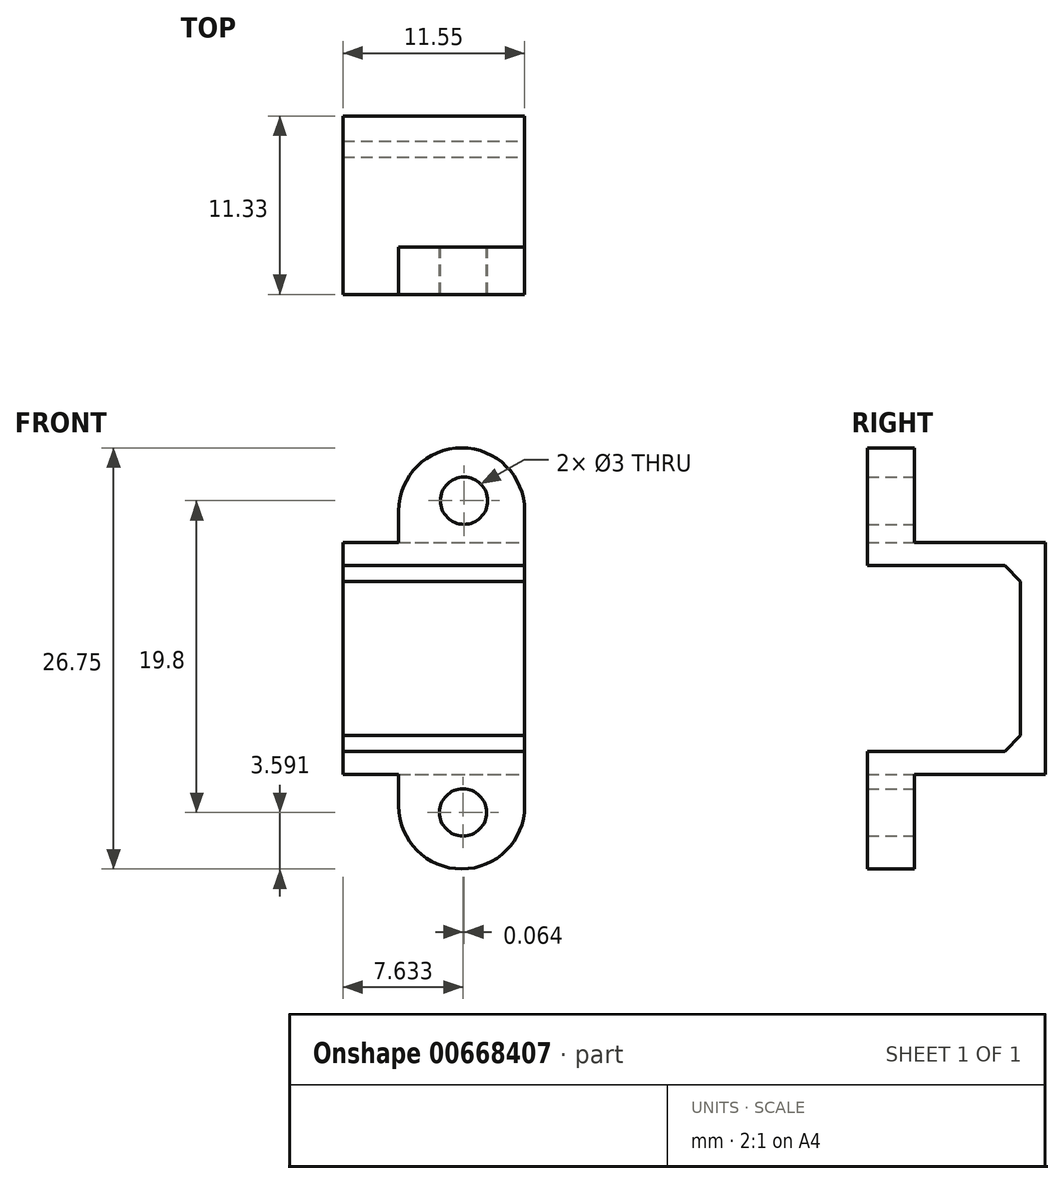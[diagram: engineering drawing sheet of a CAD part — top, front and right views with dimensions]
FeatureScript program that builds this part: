
annotation { "Feature Type Name" : "Feature", "Feature Type Description" : "" }
export const myFeature = defineFeature(function(context is Context, id is Id, definition is map)
    precondition{}
    {
        {
            var Q0;
            Q0=qCreatedBy(makeId("Front.planeOp"),FACE);
            var sketch = newSketch(context, id + "F0", { "sketchPlane" : qUnion([Q0])});
            skLineSegment(sketch, "E0.bottom", {"start": v(0, 0) * mm, "end": v(11.55, 0) * mm});
            skLineSegment(sketch, "E0.top", {"start": v(0, 14.75) * mm, "end": v(11.55, 14.75) * mm});
            skLineSegment(sketch, "E0.left", {"start": v(0, 0) * mm, "end": v(0, 14.75) * mm});
            skLineSegment(sketch, "E0.right", {"start": v(11.55, 0) * mm, "end": v(11.55, 14.75) * mm});
            skLineSegment(sketch, "E1", {"start": v(0, 14.75) * mm, "end": v(0, 13.27) * mm});
            skLineSegment(sketch, "E2", {"start": v(0, 13.27) * mm, "end": v(11.55, 13.27) * mm});
            skLineSegment(sketch, "E3", {"start": v(0, 0) * mm, "end": v(0, 1.48) * mm});
            skLineSegment(sketch, "E4", {"start": v(0, 1.48) * mm, "end": v(11.55, 1.48) * mm});
            skLineSegment(sketch, "E5", {"start": v(11.55, 1.48) * mm, "end": v(11.55, 0) * mm});
            skSolve(sketch);
        }
        {
            var Q0;
            Q0=makeQuery(id+"F0.imprint","IMPRINT",FACE,{"disambiguationData":[TD([[makeQuery(id+"F0.imprint","IMPRINT",EDGE,{"derivedFrom":sQuery(id+"F0.wireOp",EDGE,"E0.bottom")}),1.0]])]});
            var Q1;
            {var subQ0=sQuery(id+"F0.wireOp",EDGE,"E0.top");Q1=makeQuery(id+"F0.imprint","IMPRINT",FACE,{"disambiguationData":[TD([[makeQuery(id+"F0.imprint","IMPRINT",EDGE,{"derivedFrom":subQ0}),-1.0]])]});}
            var Q2;
            Q2=makeQuery(id+"F0.imprint","IMPRINT",FACE,{"disambiguationData":[TD([[makeQuery(id+"F0.imprint","IMPRINT",EDGE,{"derivedFrom":sQuery(id+"F0.wireOp",EDGE,"E0.left")}),-1.0]])]});
            extrude(context, id + "F1", {"entities" : qUnion([Q0, Q1, Q2]), "depth" : 11.33 * mm, "offsetDistance" : 25 * mm});
        }
        {
            var Q0;
            Q0=makeQuery(id+"F1.opExtrude","CAP_FACE",FACE,{"disambiguationData":[OSD([sQuery(id+"F0.wireOp",EDGE,"E0.bottom"),sQuery(id+"F0.wireOp",EDGE,"E0.top"),sQuery(id+"F0.wireOp",EDGE,"E0.left"),sQuery(id+"F0.wireOp",EDGE,"E0.right"),sQuery(id+"F0.wireOp",EDGE,"E1"),sQuery(id+"F0.wireOp",EDGE,"E3"),sQuery(id+"F0.wireOp",EDGE,"E5")])],"isStart":false});
            var sketch = newSketch(context, id + "F2", { "sketchPlane" : qUnion([Q0])});
            skLineSegment(sketch, "E6", {"start": v(0, 14.75) * mm, "end": v(0, 13.27) * mm});
            skLineSegment(sketch, "E7", {"start": v(0, 13.27) * mm, "end": v(11.55, 13.27) * mm});
            skLineSegment(sketch, "E8", {"start": v(0, 0) * mm, "end": v(0, 1.48) * mm});
            skLineSegment(sketch, "E9", {"start": v(0, 1.48) * mm, "end": v(11.55, 1.48) * mm});
            skLineSegment(sketch, "E10", {"start": v(0, 13.27) * mm, "end": v(0, 1.48) * mm});
            skLineSegment(sketch, "E11", {"start": v(11.55, 13.27) * mm, "end": v(11.55, 1.48) * mm});
            skSolve(sketch);
        }
        {
            var Q0;
            Q0=makeQuery(id+"F2.imprint","IMPRINT",FACE,{"disambiguationData":[TD([[makeQuery(id+"F2.imprint","IMPRINT",EDGE,{"derivedFrom":sQuery(id+"F2.wireOp",EDGE,"E7")}),-1.0]])]});
            extrude(context, id + "F3", {"entities" : qUnion([Q0]), "operationType" : NewBodyOperationType.REMOVE, "oppositeDirection" : true, "depth" : 9.73 * mm, "offsetDistance" : 25 * mm});
        }
        {
            var Q0;
            Q0=makeQuery(id+"F1.opExtrude","SWEPT_FACE",FACE,{"disambiguationData":[OSD([sQuery(id+"F0.wireOp",EDGE,"E0.right"),sQuery(id+"F0.wireOp",EDGE,"E5")])]});
            var sketch = newSketch(context, id + "F4", { "sketchPlane" : qUnion([Q0])});
            skLineSegment(sketch, "E12", {"start": v(-11.33, 14.75) * mm, "end": v(-11.33, 20.75) * mm});
            skLineSegment(sketch, "E13", {"start": v(-11.33, 20.75) * mm, "end": v(-8.33, 20.75) * mm});
            skLineSegment(sketch, "E14", {"start": v(-8.33, 20.75) * mm, "end": v(-8.33, 14.75) * mm});
            skLineSegment(sketch, "E15", {"start": v(-8.33, 14.75) * mm, "end": v(-11.33, 14.75) * mm});
            skSolve(sketch);
        }
        {
            var Q0;
            Q0=makeQuery(id+"F4.imprint","IMPRINT",FACE,{"disambiguationData":[TD([[makeQuery(id+"F4.imprint","IMPRINT",EDGE,{"derivedFrom":sQuery(id+"F4.wireOp",EDGE,"E12")}),-1.0]])]});
            var Q1;
            {var subQ5=sQuery(id+"F4.wireOp",EDGE,"E15");Q1=makeQuery(id+"F4.imprint","IMPRINT",FACE,{"disambiguationData":[TD([[makeQuery(id+"F4.imprint","IMPRINT",EDGE,{"derivedFrom":subQ5}),-1.0]])]});}
            extrude(context, id + "F5", {"entities" : qUnion([Q0, Q1]), "operationType" : NewBodyOperationType.ADD, "oppositeDirection" : true, "depth" : 8 * mm, "offsetDistance" : 25 * mm});
        }
        {
            var Q0;
            {var subQ0=sQuery(id+"F0.wireOp",EDGE,"E5");var subQ1=sQuery(id+"F0.wireOp",EDGE,"E0.right");Q0=makeQuery(id+"F5.boolean.opBoolean","MERGE",FACE,{"derivedFrom":[makeQuery(id+"F1.opExtrude","SWEPT_FACE",FACE,{"disambiguationData":[OSD([subQ1,subQ0])]}),makeQuery(id+"F5.opExtrude","CAP_FACE",FACE,{"disambiguationData":[OSD([sQuery(id+"F0.wireOp",EDGE,"E0.bottom"),sQuery(id+"F0.wireOp",EDGE,"E0.top"),subQ1,subQ0,sQuery(id+"F2.wireOp",EDGE,"E7"),sQuery(id+"F2.wireOp",EDGE,"E9"),sQuery(id+"F2.wireOp",EDGE,"E11"),sQuery(id+"F4.wireOp",EDGE,"E12"),sQuery(id+"F4.wireOp",EDGE,"E13"),sQuery(id+"F4.wireOp",EDGE,"E14")])],"isStart":true})]});}
            var sketch = newSketch(context, id + "F6", { "sketchPlane" : qUnion([Q0])});
            skLineSegment(sketch, "E16", {"start": v(-11.33, 0) * mm, "end": v(-11.33, -6) * mm});
            skLineSegment(sketch, "E17", {"start": v(-11.33, -6) * mm, "end": v(-8.33, -6) * mm});
            skLineSegment(sketch, "E18", {"start": v(-8.33, -6) * mm, "end": v(-8.33, 0) * mm});
            skLineSegment(sketch, "E19", {"start": v(-8.33, 0) * mm, "end": v(-11.33, 0) * mm});
            skSolve(sketch);
        }
        {
            var Q0;
            Q0=makeQuery(id+"F6.imprint","IMPRINT",FACE,{"disambiguationData":[TD([[makeQuery(id+"F6.imprint","IMPRINT",EDGE,{"derivedFrom":sQuery(id+"F6.wireOp",EDGE,"E16")}),1.0]])]});
            extrude(context, id + "F7", {"entities" : qUnion([Q0]), "operationType" : NewBodyOperationType.ADD, "oppositeDirection" : true, "depth" : 8 * mm, "offsetDistance" : 25 * mm});
        }
        {
            var Q0;
            Q0=makeQuery(id+"F5.opExtrude","CAP_EDGE",EDGE,{"disambiguationData":[OSD([sQuery(id+"F4.wireOp",EDGE,"E13")])],"isStart":true});
            fillet(context, id + "F8", {"entities" : qUnion([Q0]), "radius" : 4 * mm, "tangentPropagation" : true, "allowEdgeOverflow" : false});
        }
        {
            var Q0;
            Q0=makeQuery(id+"F5.opExtrude","CAP_EDGE",EDGE,{"disambiguationData":[OSD([sQuery(id+"F4.wireOp",EDGE,"E13")])],"isStart":false});
            fillet(context, id + "F9", {"entities" : qUnion([Q0]), "radius" : 4 * mm, "tangentPropagation" : true, "allowEdgeOverflow" : false});
        }
        {
            var Q0;
            Q0=makeQuery(id+"F7.opExtrude","CAP_EDGE",EDGE,{"disambiguationData":[OSD([sQuery(id+"F6.wireOp",EDGE,"E17")])],"isStart":true});
            fillet(context, id + "F10", {"entities" : qUnion([Q0]), "radius" : 4 * mm, "tangentPropagation" : true, "allowEdgeOverflow" : false});
        }
        {
            var Q0;
            Q0=makeQuery(id+"F7.opExtrude","CAP_EDGE",EDGE,{"disambiguationData":[OSD([sQuery(id+"F6.wireOp",EDGE,"E17")])],"isStart":false});
            fillet(context, id + "F11", {"entities" : qUnion([Q0]), "radius" : 4 * mm, "tangentPropagation" : true, "allowEdgeOverflow" : false});
        }
        {
            var Q0;
            Q0=makeQuery(id+"F7.opExtrude","SWEPT_FACE",FACE,{"disambiguationData":[OSD([sQuery(id+"F6.wireOp",EDGE,"E18")])]});
            var sketch = newSketch(context, id + "F12", { "sketchPlane" : qUnion([Q0])});
            skCircle(sketch, "E20", {"center": v(-7.63, -2.4) * mm, "radius": 1.5 * mm});
            skSolve(sketch);
        }
        {
            var Q0;
            Q0 = qSketchRegion(id + "F12", true);
            extrude(context, id + "F13", {"entities" : qUnion([Q0]), "operationType" : NewBodyOperationType.REMOVE, "oppositeDirection" : true, "depth" : 25 * mm, "offsetDistance" : 25 * mm});
        }
        {
            var Q0;
            Q0=makeQuery(id+"F5.opExtrude","SWEPT_FACE",FACE,{"disambiguationData":[OSD([sQuery(id+"F4.wireOp",EDGE,"E14")])]});
            var sketch = newSketch(context, id + "F14", { "sketchPlane" : qUnion([Q0])});
            skCircle(sketch, "E21", {"center": v(-7.7, 17.4) * mm, "radius": 1.5 * mm});
            skSolve(sketch);
        }
        {
            var Q0;
            Q0 = qSketchRegion(id + "F14", true);
            extrude(context, id + "F15", {"entities" : qUnion([Q0]), "operationType" : NewBodyOperationType.REMOVE, "oppositeDirection" : true, "depth" : 25 * mm, "offsetDistance" : 25 * mm});
        }
        {
            var Q0;
            Q0=makeQuery(id+"F3.boolean.opBoolean","COPY",EDGE,{"derivedFrom":makeQuery(id+"F3.opExtrude","CAP_EDGE",EDGE,{"disambiguationData":[OSD([sQuery(id+"F2.wireOp",EDGE,"E7")])],"isStart":false})});
            chamfer(context, id + "F16", {"entities" : qUnion([Q0]), "width" : 1 * mm, "tangentPropagation" : true});
        }
        {
            var Q0;
            Q0=makeQuery(id+"F3.boolean.opBoolean","COPY",EDGE,{"derivedFrom":makeQuery(id+"F3.opExtrude","CAP_EDGE",EDGE,{"disambiguationData":[OSD([sQuery(id+"F2.wireOp",EDGE,"E9")])],"isStart":false})});
            chamfer(context, id + "F17", {"entities" : qUnion([Q0]), "width" : 1 * mm, "tangentPropagation" : true});
        }
    });
